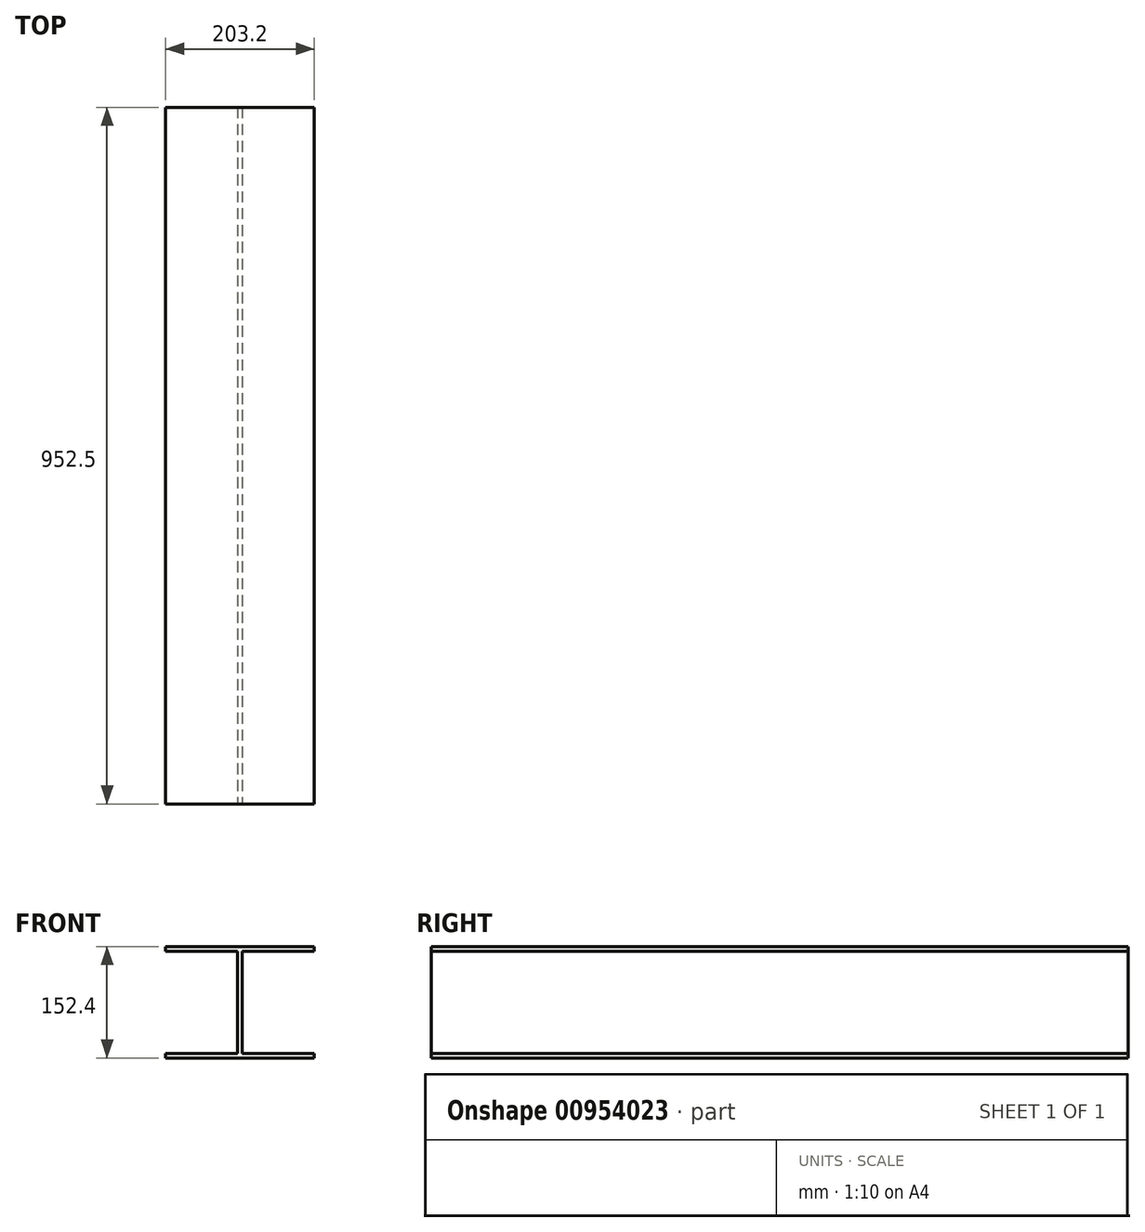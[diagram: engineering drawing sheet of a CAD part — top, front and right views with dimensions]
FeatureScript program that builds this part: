
annotation { "Feature Type Name" : "Feature", "Feature Type Description" : "" }
export const myFeature = defineFeature(function(context is Context, id is Id, definition is map)
    precondition{}
    {
        {
            var Q0;
            Q0=qCreatedBy(makeId("Front.planeOp"),FACE);
            var sketch = newSketch(context, id + "F0", { "sketchPlane" : qUnion([Q0])});
            skLineSegment(sketch, "E0.bottom", {"start": v(-101.6, 0) * mm, "end": v(101.6, 0) * mm});
            skLineSegment(sketch, "E0.top", {"start": v(-101.6, 152.4) * mm, "end": v(101.6, 152.4) * mm});
            skLineSegment(sketch, "E0.left", {"start": v(-101.6, 0) * mm, "end": v(-101.6, 6.35) * mm});
            skLineSegment(sketch, "E0.right", {"start": v(101.6, 0) * mm, "end": v(101.6, 6.35) * mm});
            skLineSegment(sketch, "E1.bottom", {"start": v(101.6, 146.05) * mm, "end": v(3.18, 146.05) * mm});
            skLineSegment(sketch, "E1.top", {"start": v(101.6, 6.35) * mm, "end": v(3.18, 6.35) * mm});
            skLineSegment(sketch, "E1.right", {"start": v(3.18, 146.05) * mm, "end": v(3.18, 6.35) * mm});
            skLineSegment(sketch, "E2.bottom", {"start": v(-101.6, 6.35) * mm, "end": v(-3.17, 6.35) * mm});
            skLineSegment(sketch, "E2.top", {"start": v(-101.6, 146.05) * mm, "end": v(-3.18, 146.05) * mm});
            skLineSegment(sketch, "E2.right", {"start": v(-3.18, 6.35) * mm, "end": v(-3.18, 146.05) * mm});
            skLineSegment(sketch, "E3.trimOffspring", {"start": v(-101.6, 146.05) * mm, "end": v(-101.6, 152.4) * mm});
            skLineSegment(sketch, "E4.trimOffspring", {"start": v(101.6, 146.05) * mm, "end": v(101.6, 152.4) * mm});
            skSolve(sketch);
        }
        {
            var Q0;
            Q0=makeQuery(id+"F0.imprint","IMPRINT",FACE,{"disambiguationData":[TD([[makeQuery(id+"F0.imprint","IMPRINT",EDGE,{"derivedFrom":sQuery(id+"F0.wireOp",EDGE,"E0.bottom")}),1.0]])]});
            extrude(context, id + "F1", {"entities" : qUnion([Q0]), "oppositeDirection" : true, "depth" : 952.5 * mm, "offsetDistance" : 25.4 * mm});
        }
    });
